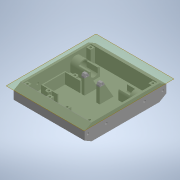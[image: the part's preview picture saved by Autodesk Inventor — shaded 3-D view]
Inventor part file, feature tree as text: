
AUTODESK INVENTOR PART (.ipt)
format: ipt  version: 2020 (Build 240168000, 168)  size: 516,096 bytes
history: native  units: in
note: dims shown in document units (in); Inventor stores cm internally (conversion verified against a paired STEP export)
features: sketch x15, projected_geometry x15, extrude x14, mirror x4, plane x2
ambient origin geometry x8: Origin, YZ Plane, XZ Plane, XY Plane, X Axis, Y Axis, Z Axis, Center Point
bodies: Solid1 (feature_tree)
feature tree (50):
  extrude  "Extrusion1"  Depth=5.9055in
  extrude  "Extrusion2"  TaperAngle=0.0deg  [1 undecoded]
  extrude  "Extrusion3"  Depth=1.063in
  extrude  "Extrusion4"  Depth=0.315in
  extrude  "Extrusion5"  TaperAngle=0.0deg  [1 undecoded]
  extrude  "Extrusion6"  Depth=0.5906in
  mirror  "Mirror1"
  extrude  "Extrusion7"  Depth=0.0787in
  mirror  "Mirror2"
  extrude  "Extrusion8"  Depth=0.6102in
  mirror  "Mirror3"
  plane  "Work Plane1"
  extrude  "Extrusion9"  Depth=0.7874in TaperAngle=0.0deg
  mirror  "Mirror4"
  extrude  "Extrusion10"  Depth=6.063in TaperAngle=0.0deg
  extrude  "Extrusion11"  Depth=0.1575in
  extrude  "Extrusion12"  TaperAngle=0.0deg  [1 undecoded]
  extrude  "Extrusion13"  Depth=0.2756in
  extrude  "Extrusion14"  Depth=0.4331in
  plane  "Work Plane2"
  sketch  "Sketch18"  dims[d34=0.122in d38=2.7559in d40=0.061in d41=0.0909in d42=0.2362in d43=0.0in d44=60.0deg d45=0.0787in d46=0.315in d48=0.993in d49=0.0in d51=0.1575in d52=0.1575in d53=0.2756in d54=0.0in d55=0.4724in d56=1.1614in d57=1.5748in d58=1.5945in d59=0.0787in d60=0.0787in d62=0.315in d63=0.7677in d64=0.0in d65=0.1575in d66=0.1575in d67=0.2756in d68=0.0in d69=0.8268in d70=0.2953in d71=0.0394in d72=0.0in d76=0.1575in d77=120.0deg d79=0.1969in d80=0.1969in d81=0.1969in d82=0.1969in d83=0.1969in d85=120.0deg]
  sketch  "Sketch1"  dims[d0=1.1811in d1=5.9055in]
  sketch  "Sketch2"  dims[d2=5.1181in d3=0.0in]
  projected_geometry  "Projected Loop1"
  sketch  "Sketch3"  dims[d4=0.1575in d5=1.063in]
  projected_geometry  "Projected Loop2"
  projected_geometry  "Projected Loop3"
  sketch  "Sketch4"  dims[d6=0.0in d8=0.315in]
  sketch  "Sketch5"  dims[d10=0.993in d11=0.0in]
  projected_geometry  "Projected Loop4"
  sketch  "Sketch6"  dims[d12=0.6496in d13=0.5906in]
  sketch  "Sketch7"  dims[d14=1.5748in d15=0.0787in]
  sketch  "Sketch9"  dims[d16=0.5512in d17=0.0in d18=0.6102in]
  sketch  "Sketch10"  dims[d19=0.4803in d20=0.7874in d21=0.0in]
  sketch  "Sketch12"  dims[d22=0.1654in d23=6.063in d24=0.0in]
  projected_geometry  "Projected Loop6"
  projected_geometry  "Projected Loop7"
  projected_geometry  "Projected Loop8"
  sketch  "Sketch13"  dims[d25=0.5114in d26=0.1575in]
  projected_geometry  "Projected Loop9"
  projected_geometry  "Projected Loop10"
  projected_geometry  "Projected Loop11"
  projected_geometry  "Projected Loop12"
  projected_geometry  "Projected Loop13"
  projected_geometry  "Projected Loop14"
  sketch  "Sketch14"  dims[d27=1.5748in d28=0.0in d29=0.0in]
  sketch  "Sketch15"  dims[d30=0.1575in d31=0.2756in]
  projected_geometry  "Projected Loop15"
  sketch  "Sketch16"  dims[d32=0.0in d33=0.4331in]
  projected_geometry  "Projected Loop18"
note: 3 required parameter values undecoded (feature->parameter linkage not recoverable at this tier; creation-order binding heuristic only, values carry confidence <= 0.55)
